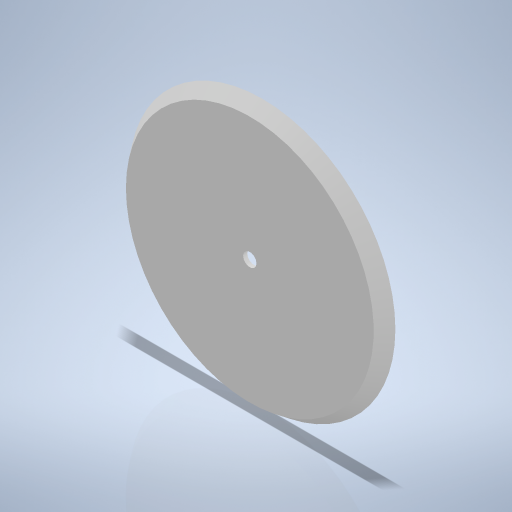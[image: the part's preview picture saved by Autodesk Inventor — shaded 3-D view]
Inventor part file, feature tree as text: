
AUTODESK INVENTOR PART (.ipt)
format: ipt  version: 2024 (Build 280153000, 153)  size: 236,032 bytes
history: native  units: mm
features: sketch x2, revolve x1, shell x1, extrude x1
ambient origin geometry x8: Origin, YZ Plane, XZ Plane, XY Plane, X Axis, Y Axis, Z Axis, Center Point
bodies: Volumenkörper1 (feature_tree)
feature tree (5):
  revolve  "Umdrehung1"
  shell  "Wandung1"  Thickness=31.0mm
  extrude  "Extrusion1"  Depth=1.0mm
  sketch  "Skizze1"  dims[d2=29.5mm d3=1.0mm]
  sketch  "Skizze2"  dims[d4=90.0deg d5=1.62mm d6=10.0mm d7=0.0mm d8=0.5mm]
